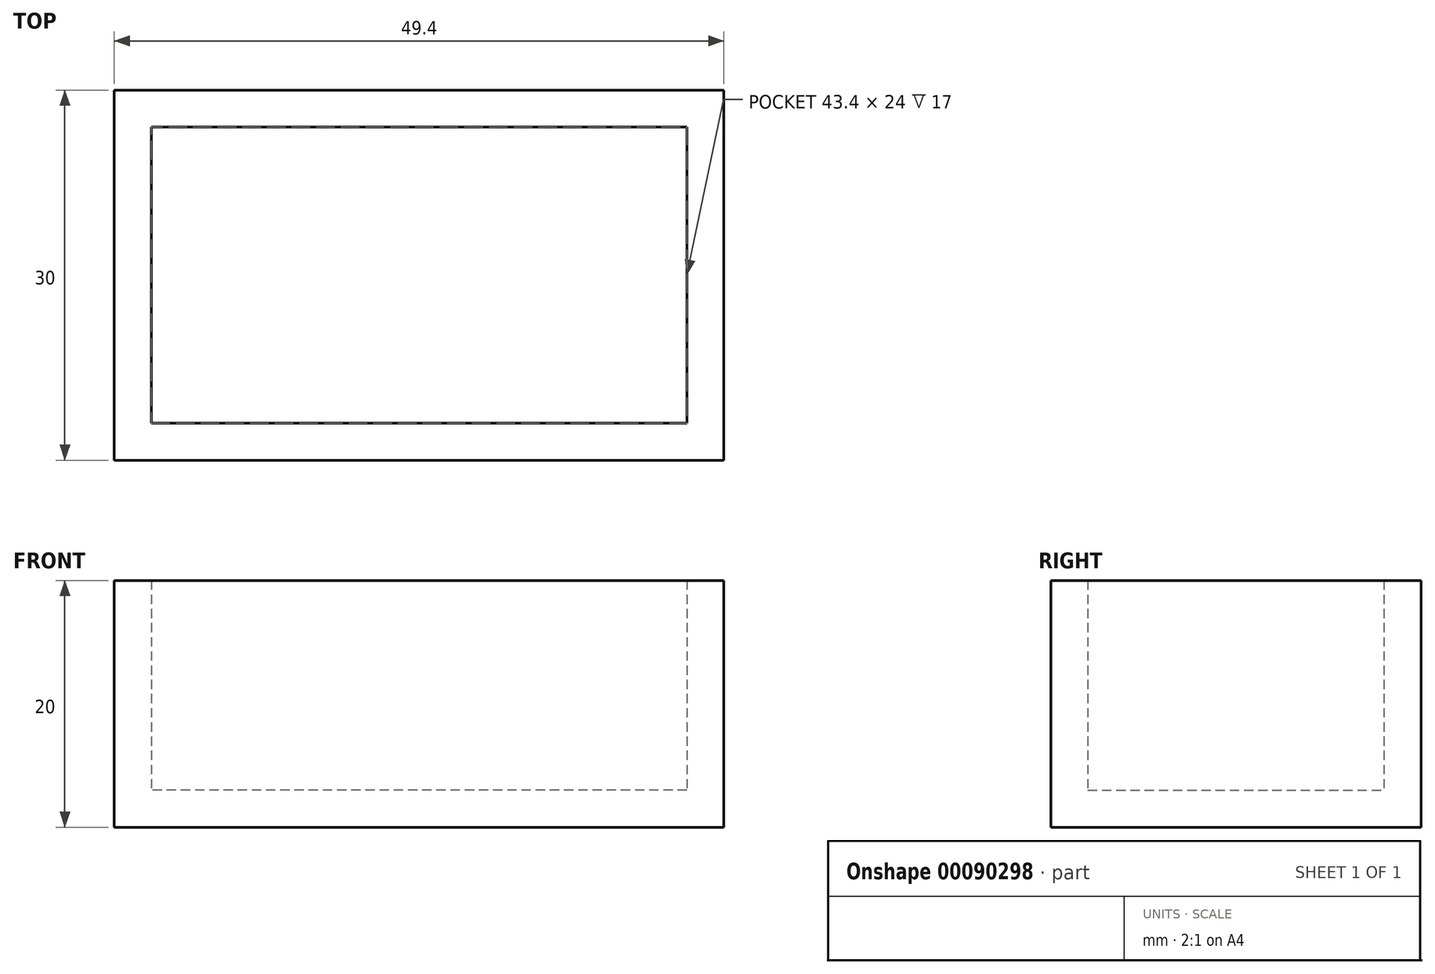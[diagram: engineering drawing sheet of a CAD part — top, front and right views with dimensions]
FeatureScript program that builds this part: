
annotation { "Feature Type Name" : "Feature", "Feature Type Description" : "" }
export const myFeature = defineFeature(function(context is Context, id is Id, definition is map)
    precondition{}
    {
        {
            var Q0;
            Q0=qCreatedBy(makeId("Top.planeOp"),FACE);
            var sketch = newSketch(context, id + "F0", { "sketchPlane" : qUnion([Q0])});
            skLineSegment(sketch, "E0", {"start": v(0, 14) * mm, "end": v(-24.7, 14) * mm});
            skLineSegment(sketch, "E1", {"start": v(-21.7, -13) * mm, "end": v(-21.7, 11) * mm});
            skLineSegment(sketch, "E2", {"start": v(0, 18.97) * mm, "end": v(0, -27.48) * mm, "construction": true});
            skLineSegment(sketch, "E3", {"start": v(-24.7, 14) * mm, "end": v(-24.7, -6) * mm});
            skLineSegment(sketch, "E4", {"start": v(-24.7, -9.43) * mm, "end": v(-24.7, -13) * mm});
            skLineSegment(sketch, "E5", {"start": v(-21.7, 11) * mm, "end": v(0, 11) * mm});
            skLineSegment(sketch, "E6.MirrorCS", {"start": v(0, 14) * mm, "end": v(24.7, 14) * mm});
            skLineSegment(sketch, "E7.MirrorCS", {"start": v(21.7, 11) * mm, "end": v(0, 11) * mm});
            skLineSegment(sketch, "E8.MirrorCS", {"start": v(24.7, 14) * mm, "end": v(24.7, -6) * mm});
            skLineSegment(sketch, "E9.MirrorCS", {"start": v(21.7, -13) * mm, "end": v(21.7, 11) * mm});
            skLineSegment(sketch, "E10.MirrorCS", {"start": v(24.7, -9.43) * mm, "end": v(24.7, -13) * mm});
            skLineSegment(sketch, "E11", {"start": v(-24.7, -6) * mm, "end": v(-24.7, -9.43) * mm});
            skLineSegment(sketch, "E12", {"start": v(24.7, -6) * mm, "end": v(24.7, -9.43) * mm});
            skLineSegment(sketch, "E13", {"start": v(-21.7, -16) * mm, "end": v(-24.7, -16) * mm});
            skLineSegment(sketch, "E14", {"start": v(-24.7, -16) * mm, "end": v(-24.7, -13) * mm});
            skLineSegment(sketch, "E15", {"start": v(-21.7, -13) * mm, "end": v(21.7, -13) * mm});
            skLineSegment(sketch, "E16", {"start": v(21.7, -16) * mm, "end": v(24.7, -16) * mm});
            skLineSegment(sketch, "E17", {"start": v(24.7, -16) * mm, "end": v(24.7, -13) * mm});
            skLineSegment(sketch, "E18", {"start": v(21.7, -16) * mm, "end": v(-21.7, -16) * mm});
            skSolve(sketch);
        }
        {
            var Q0;
            Q0=makeQuery(id+"F0.imprint","IMPRINT",FACE,{"disambiguationData":[TD([[makeQuery(id+"F0.imprint","IMPRINT",EDGE,{"derivedFrom":sQuery(id+"F0.wireOp",EDGE,"E0")}),1.0]])]});
            extrude(context, id + "F1", {"entities" : qUnion([Q0]), "depth" : 20 * mm});
        }
        {
            var Q0;
            Q0=makeQuery(id+"F0.imprint","IMPRINT",FACE,{"disambiguationData":[TD([[makeQuery(id+"F0.imprint","IMPRINT",EDGE,{"derivedFrom":sQuery(id+"F0.wireOp",EDGE,"E1")}),-1.0]])]});
            extrude(context, id + "F2", {"entities" : qUnion([Q0]), "operationType" : NewBodyOperationType.ADD, "depth" : 3 * mm});
        }
    });
